SOLIDWORKS PART (.sldprt)
format: sldprt  version: not decoded by parser v0  size: 601,600 bytes
history: native  units: mm
features: sketch x5, plane x3, material x1, extrude x1, chamfer x1, revolve x1, cut_extrude x1, helix x1, sweep x1 (+10 scaffold rows collapsed)
feature tree (25):
  scaffold x10  (default folders/planes/origin — collapsed)
  material  "Matériau <non spécifié>"
  plane  "Plan1"
  plane  "Plan2"
  plane  "Plan3"
  sketch  "Esquisse2"  dims[Diamètre nominal=3.0mm]
  extrude  "Tige"  Depth=6mm Longueur sous tête=6mm
  chamfer  "Chanfrein d'entrée"  Distance=0.5mm Angle=45deg Pas=0.5mm
  sketch  "Esquisse5"  dims[c1.D2=0.18mm c1.Hauteur tête=2.0mm c1.Cote sur plats=5.5mm c1.D3=~2.780036mm c2.D3=30.0deg c2.D4=2.75mm c2.Diamètre tête=5.5mm c2.Diamètre nominal=3.0mm c2.D1=2.75mm c3.D3=3.0mm c4.D3=60.0deg c4.Hauteur tête=1.8mm c4.Cote sur plats=2.5mm c4.D4=1.5mm c4.D5=1.25mm]
  revolve  "Tête"  Angle=360deg
  sketch  "Esquisse6"  dims[Largeur fente=0.8mm]
  cut_extrude  "Fente"  Depth=0.9mm
  sketch  "Esquisse7"
  helix  "Hélice1"  Pitch=5.625mm Longueur filetée=5.625mm Pas=0.5mm
  sketch  "Esquisse8"  dims[c1.D1=2.4mm c2.D1=29.5deg c2.Pas=0.5mm c3.D1=0.55mm c3.D2=2.4mm c4.D2=29.5deg c4.D3=~5.999444mm c5.D3=90.0deg c6.D3=~1.066987mm c6.D4=~0.293538mm c6.D5=~0.38293mm c7.D4=0.25mm c7.Pas=0.5mm]
  sweep  "Filetage"
decode coverage: 9 of 11 modeling features carry decoded parameters
note: ~ marks probable driven/reference dimensions
note: suppression state not decoded; provenance and decode notes live in map.json
